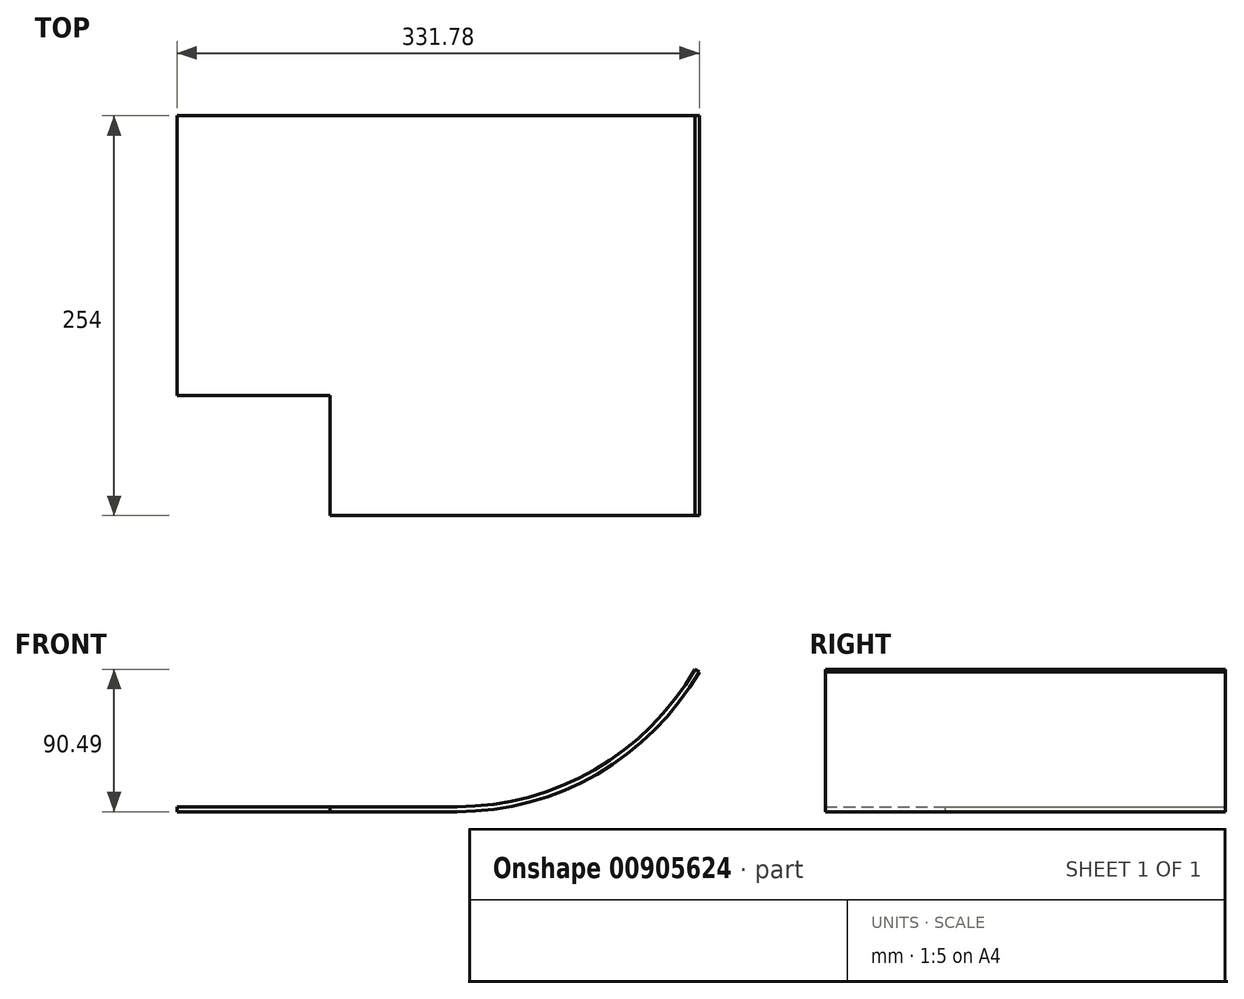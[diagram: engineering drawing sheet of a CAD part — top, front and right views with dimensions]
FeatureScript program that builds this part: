
annotation { "Feature Type Name" : "Feature", "Feature Type Description" : "" }
export const myFeature = defineFeature(function(context is Context, id is Id, definition is map)
    precondition{}
    {
        {
            var Q0;
            Q0=qCreatedBy(makeId("Front.planeOp"),FACE);
            var sketch = newSketch(context, id + "F0", { "sketchPlane" : qUnion([Q0])});
            skLineSegment(sketch, "E0", {"start": v(-97.13, -14.48) * mm, "end": v(80.67, -14.48) * mm});
            skArc(sketch, "E1", {"start": v(80.67, -14.48) * mm, "mid": v(169.57, 9.34) * mm, "end": v(234.65, 74.42) * mm});
            skArc(sketch, "E2.0", {"start": v(80.67, -11.3) * mm, "mid": v(167.99, 12.09) * mm, "end": v(231.9, 76) * mm});
            skLineSegment(sketch, "E2.1", {"start": v(-97.13, -11.3) * mm, "end": v(80.67, -11.3) * mm});
            skLineSegment(sketch, "E3", {"start": v(231.9, 76) * mm, "end": v(234.65, 74.42) * mm});
            skLineSegment(sketch, "E4", {"start": v(-97.13, -14.48) * mm, "end": v(-97.13, -11.3) * mm});
            skSolve(sketch);
        }
        {
            var Q0;
            Q0 = qSketchRegion(id + "F0", true);
            extrude(context, id + "F1", {"entities" : qUnion([Q0]), "depth" : 177.8 * mm, "offsetDistance" : 25.4 * mm});
        }
        {
            var Q0;
            Q0=makeQuery(id+"F1.opExtrude","CAP_FACE",FACE,{"disambiguationData":[OSD([sQuery(id+"F0.wireOp",EDGE,"E0"),sQuery(id+"F0.wireOp",EDGE,"E1"),sQuery(id+"F0.wireOp",EDGE,"E2.0"),sQuery(id+"F0.wireOp",EDGE,"E2.1"),sQuery(id+"F0.wireOp",EDGE,"E3"),sQuery(id+"F0.wireOp",EDGE,"E4")])],"isStart":false});
            var sketch = newSketch(context, id + "F2", { "sketchPlane" : qUnion([Q0])});
            skLineSegment(sketch, "E5", {"start": v(0, -11.3) * mm, "end": v(0, -14.48) * mm});
            skLineSegment(sketch, "E6", {"start": v(0, -14.48) * mm, "end": v(25.07, -14.48) * mm});
            skLineSegment(sketch, "E7", {"start": v(25.07, -14.48) * mm, "end": v(80.67, -14.48) * mm});
            skLineSegment(sketch, "E8", {"start": v(0, -11.3) * mm, "end": v(80.67, -11.3) * mm});
            skArc(sketch, "E9", {"start": v(80.67, -11.3) * mm, "mid": v(167.99, 12.09) * mm, "end": v(231.9, 76) * mm});
            skArc(sketch, "E10", {"start": v(80.67, -14.48) * mm, "mid": v(169.57, 9.34) * mm, "end": v(234.65, 74.42) * mm});
            skLineSegment(sketch, "E11", {"start": v(231.9, 76) * mm, "end": v(234.65, 74.42) * mm});
            skSolve(sketch);
        }
        {
            var Q0;
            Q0 = qSketchRegion(id + "F2", true);
            extrude(context, id + "F3", {"entities" : qUnion([Q0]), "operationType" : NewBodyOperationType.ADD, "depth" : 76.2 * mm, "offsetDistance" : 25.4 * mm});
        }
    });
